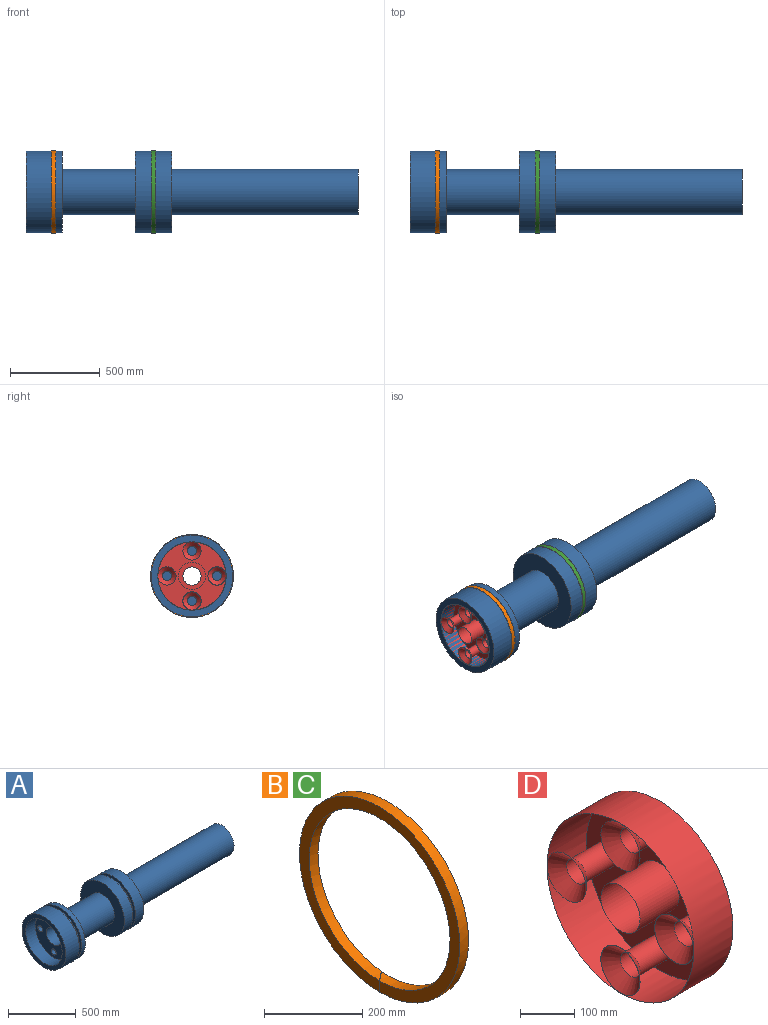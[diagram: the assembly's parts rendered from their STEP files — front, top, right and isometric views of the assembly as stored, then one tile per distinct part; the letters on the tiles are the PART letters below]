
ASSEMBLY  parts=4 mates=3
PART A: 30 faces, bbox 1854.2x457.2x457.2 mm
  f0: cylinder r=203.2mm len=406.4mm, axis (-1,0,0), area 32429.3mm2, adj f3,f14
  f1: cylinder r=228.6mm len=457.2mm, axis (1,0,0), area 127690.3mm2, adj f2,f3
  f2: plane 457.2x457.2mm, normal (-1,0,0), area 113502.5mm2, adj f1,f4
  f3: plane 457.2x457.2mm, normal (1,0,0), area 34456.1mm2, adj f0,f1
  f4: cylinder r=127mm len=406.4mm, axis (1,0,0), area 324292.8mm2, adj f2,f7
  f5: cylinder r=228.6mm len=457.2mm, axis (1,0,0), area 54724.4mm2, adj f6,f7
  f6: plane 457.2x457.2mm, normal (-1,0,0), area 34456.1mm2, adj f5,f8
  f7: plane 457.2x457.2mm, normal (1,0,0), area 113502.5mm2, adj f4,f5
  f8: cylinder r=203.2mm len=406.4mm, axis (1,0,0), area 32429.3mm2, adj f6,f11
  f9: cylinder r=228.6mm len=457.2mm, axis (1,0,0), area 200656.2mm2, adj f10,f11
  f10: plane 457.2x457.2mm, normal (-1,0,0), area 50164mm2, adj f9,f17
  f11: plane 457.2x457.2mm, normal (1,0,0), area 34456.1mm2, adj f8,f9
  f12: cylinder r=228.6mm len=457.2mm, axis (-1,0,0), area 127690.3mm2, adj f13,f14
  f13: plane 457.2x457.2mm, normal (1,0,0), area 113502.5mm2, adj f12,f15
  f14: plane 457.2x457.2mm, normal (-1,0,0), area 34456.1mm2, adj f0,f12
  f15: cylinder r=127mm len=1041.4mm, axis (-1,0,0), area 831000.3mm2, adj f13,f16
  f16: plane 254x254mm, normal (1,0,0), area 42563.4mm2, adj f15,f29
  f17: cylinder r=190.5mm len=381mm, axis (-1,0,0), area 121609.8mm2, adj f10,f18
  f18: plane 381x381mm, normal (-1,0,0), area 87660.4mm2, adj f17,f20,f21,f23,f25,f27
  f19: plane 152.4x152.4mm, normal (-1,0,0), area 10134.1mm2, adj f20,f29
  f20: cylinder r=76.2mm len=1701.8mm, axis (-1,0,0), area 814785.6mm2, adj f18,f19
  f21: cylinder r=25.4mm len=88.9mm, axis (-1,0,0), area 14187.8mm2, adj f18,f22
  f22: plane 50.8x50.8mm, normal (-1,0,0), area 2026.8mm2, adj f21
  f23: cylinder r=25.4mm len=88.9mm, axis (-1,0,0), area 14187.8mm2, adj f18,f24
  f24: plane 50.8x50.8mm, normal (-1,0,0), area 2026.8mm2, adj f23
  f25: cylinder r=25.4mm len=88.9mm, axis (-1,0,0), area 14187.8mm2, adj f18,f26
  f26: plane 50.8x50.8mm, normal (-1,0,0), area 2026.8mm2, adj f25
  f27: cylinder r=25.4mm len=88.9mm, axis (-1,0,0), area 14187.8mm2, adj f18,f28
  f28: plane 50.8x50.8mm, normal (-1,0,0), area 2026.8mm2, adj f27
  f29: cylinder r=50.8mm len=101.6mm, axis (1,0,0), area 16214.6mm2, adj f16,f19
PART B: 6 faces, bbox 25.4x462.3x462.3 mm
  f0: cylinder r=203.2mm len=406.4mm, axis (-1,0,0), area 32412.8mm2, adj f2,f3,f4,f5
  f1: cylinder r=231.14mm len=462.28mm, axis (-1,0,0), area 36871.8mm2, adj f2,f3,f4,f5
  f2: plane 462.28x462.28mm, normal (1,0,0), area 38106.5mm2, adj f0,f1,f4,f5
  f3: plane 462.28x462.28mm, normal (-1,0,0), area 38106.6mm2, adj f0,f1,f4,f5
  f4: plane 28.93x25.4mm, normal (-0.62,0.79,0), area 905.3mm2, adj f0,f1,f2,f3
  f5: plane 29x25.4mm, normal (0.62,-0.79,0), area 905.5mm2, adj f0,f1,f2,f3
PART C: same geometry as B
PART D: 12 faces, bbox 101.6x381x381 mm
  f0: cylinder r=25.4mm len=76.2mm, axis (-1,0,0), area 12161mm2, adj f6,f11
  f1: cylinder r=25.4mm len=76.2mm, axis (-1,0,0), area 12161mm2, adj f6,f10
  f2: cylinder r=25.4mm len=76.2mm, axis (-1,0,0), area 12161mm2, adj f6,f8
  f3: cylinder r=25.4mm len=76.2mm, axis (-1,0,0), area 12161mm2, adj f6,f9
  f4: cylinder r=50.8mm len=101.6mm, axis (-1,0,0), area 32429.3mm2, adj f6,f7
  f5: cylinder r=190.5mm len=381mm, axis (-1,0,0), area 121609.8mm2, adj f6,f7
  f6: plane 381x381mm, normal (1,0,0), area 97794.5mm2, adj f0,f1,f2,f3,f4,f5
  f7: plane 381.01x381.01mm, normal (-1,0,0), area 73472.6mm2, adj f4,f5,f8,f9,f10,f11
  f8: cone r=25.4mm half-angle=45deg, axis (-1,0,0), area 8599.1mm2, adj f2,f7
  f9: cone r=25.4mm half-angle=45deg, axis (-1,0,0), area 8599.1mm2, adj f3,f7
  f10: cone r=25.4mm half-angle=45deg, axis (-1,0,0), area 8599.1mm2, adj f1,f7
  f11: cone r=25.4mm half-angle=45deg, axis (-1,0,0), area 8599.1mm2, adj f0,f7
PLACE A t=(-18246.69,-4781.77,-2388.59)mm
PLACE B t=(-14157.29,-1073.37,-2388.59)mm
PLACE C t=(-13598.49,-1073.37,-2388.59)mm
PLACE D t=(-14246.19,374.43,-2388.59)mm
MATE fastened C.f0 <-> A.f1  axis (1,0,0) through (8702.71,3549.43,-2388.59)mm
MATE fastened D.f1 <-> A.f27  axis (1,0,0) through (8080.41,3549.43,-2248.89)mm
MATE fastened B.f0 <-> A.f1  axis (1,0,0) through (8143.91,3549.43,-2388.59)mm
